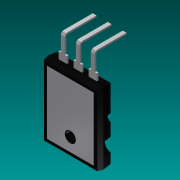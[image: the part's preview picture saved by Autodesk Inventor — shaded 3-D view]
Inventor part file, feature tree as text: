
AUTODESK INVENTOR PART (.ipt)
format: ipt  version: 2015 (Build 190159000, 159)  size: 619,520 bytes
history: native  units: mm
features: sketch x9, extrude x6, projected_geometry x5, fillet x2, hole x1, plane x1, emboss x1, sweep x1
ambient origin geometry x8: Origin, YZ Plane, XZ Plane, XY Plane, X Axis, Y Axis, Z Axis, Center Point
bodies: Solid1 (feature_tree)
feature tree (26):
  extrude  "Extrusion1"  Depth=26.0mm
  hole  "Hole1"  [1 undecoded]
  extrude  "Extrusion2"  Depth=6.0mm
  plane  "Work Plane1"
  extrude  "Extrusion3"  Depth=2.25mm
  extrude  "Extrusion4"  Depth=3.0mm
  fillet  "Fillet1"  Radius=3.0mm
  fillet  "Fillet2"  [1 undecoded]
  extrude  "Extrusion5"  Depth=3.0mm
  emboss  "Emboss1"
  extrude  "Extrusion6"  Depth=3.0mm
  sweep  "Sweep1"
  sketch  "Sketch1"  dims[d0=20.0mm d1=26.0mm]
  sketch  "Sketch2"  dims[d2=3.0mm d3=2.0mm d4=-0.872665mm d5=-1.745329mm d6=6.3mm d7=1.0mm]
  sketch  "Sketch3"  dims[d8=3.5mm d9=6.0mm d10=4.0mm d11=2.0mm d12=90.0deg d13=8.0mm d14=20.594885mm d15=4.35mm]
  sketch  "Sketch4"  dims[d16=4.35mm d17=2.25mm]
  sketch  "Sketch5"  dims[d18=2.25mm d19=11.2mm d20=3.0mm d21=0.872665mm d22=-3.0mm]
  sketch  "Sketch6"  dims[d23=3.0mm d24=5.0mm]
  sketch  "Sketch7"  dims[d25=3.0mm d26=5.0mm]
  sketch  "Sketch8"  dims[d27=3.0mm d28=5.0mm]
  sketch  "Sketch9"  dims[d29=5.45mm d30=5.45mm d31=1.4mm d32=5.0mm d33=20.0mm d35=5.45mm d36=20.0mm d38=5.45mm d41=0.3mm d42=0.3mm d43=0.0mm d44=0.0mm d45=23.0mm d46=17.0mm d47=4.0mm d48=0.001mm d49=0.0mm d50=0.2mm d51=0.2mm d52=13.0mm d53=9.0mm d54=5.0mm d55=0.1mm d56=0.0mm d57=0.2mm d58=0.0mm d59=2.5mm d60=0.2mm d61=0.1mm d62=0.0mm d63=1.0mm d64=11.0mm d65=0.599834mm d66=1.0mm d67=0.5mm d68=0.0mm d69=0.0mm]
  projected_geometry  "Project Cut Edges1"
  projected_geometry  "Project Cut Edges2"
  projected_geometry  "Project Cut Edges3"
  projected_geometry  "Project Cut Edges4"
  projected_geometry  "Project Cut Edges5"
note: 2 required parameter values undecoded (feature->parameter linkage not recoverable at this tier; creation-order binding heuristic only, values carry confidence <= 0.55)
